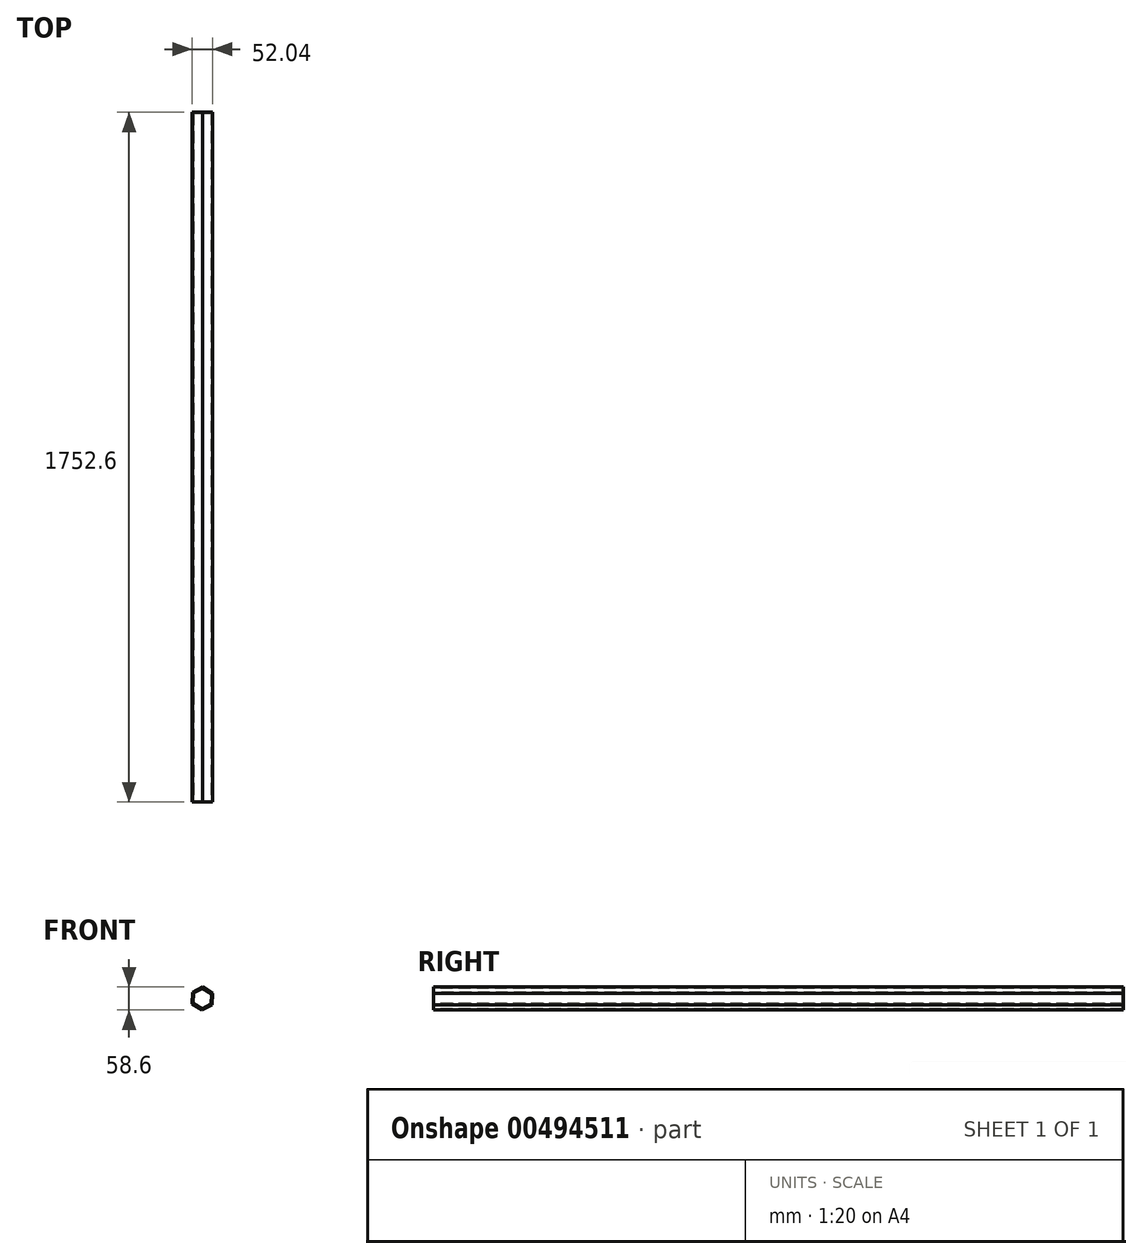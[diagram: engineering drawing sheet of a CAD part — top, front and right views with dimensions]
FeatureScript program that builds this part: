
annotation { "Feature Type Name" : "Feature", "Feature Type Description" : "" }
export const myFeature = defineFeature(function(context is Context, id is Id, definition is map)
    precondition{}
    {
        {
            var Q0;
            Q0=qCreatedBy(makeId("Front.planeOp"),FACE);
            var sketch = newSketch(context, id + "F0", { "sketchPlane" : qUnion([Q0])});
            skCircle(sketch, "E0.cCircle", {"center": v(0, 0) * mm, "radius": 25.4 * mm, "construction": true});
            skLineSegment(sketch, "E0.0", {"start": v(24.74, -15.76) * mm, "end": v(-1.28, -29.3) * mm});
            skLineSegment(sketch, "E0.1", {"start": v(-1.28, -29.3) * mm, "end": v(-26.02, -13.54) * mm});
            skLineSegment(sketch, "E0.2", {"start": v(-26.02, -13.54) * mm, "end": v(-24.74, 15.76) * mm});
            skLineSegment(sketch, "E0.3", {"start": v(-24.74, 15.76) * mm, "end": v(1.28, 29.3) * mm});
            skLineSegment(sketch, "E0.4", {"start": v(1.28, 29.3) * mm, "end": v(26.02, 13.54) * mm});
            skLineSegment(sketch, "E0.5", {"start": v(26.02, 13.54) * mm, "end": v(24.74, -15.76) * mm});
            skPoint(sketch, "E0.0.midPoint", {"position": v(11.73, -22.53) * mm});
            skSolve(sketch);
        }
        {
            var Q0;
            Q0 = qSketchRegion(id + "F0", true);
            extrude(context, id + "F1", {"entities" : qUnion([Q0]), "oppositeDirection" : true, "depth" : 1752.6 * mm});
        }
        {
            var Q0;
            Q0=makeQuery(id+"F1.opExtrude","CAP_FACE",FACE,{"disambiguationData":[OSD([sQuery(id+"F0.wireOp",EDGE,"E0.0"),sQuery(id+"F0.wireOp",EDGE,"E0.1"),sQuery(id+"F0.wireOp",EDGE,"E0.2"),sQuery(id+"F0.wireOp",EDGE,"E0.3"),sQuery(id+"F0.wireOp",EDGE,"E0.4"),sQuery(id+"F0.wireOp",EDGE,"E0.5")])],"isStart":true});
            shell(context, id + "F2", {"entities" : qUnion([Q0]), "thickness" : 2.54 * mm});
        }
    });
